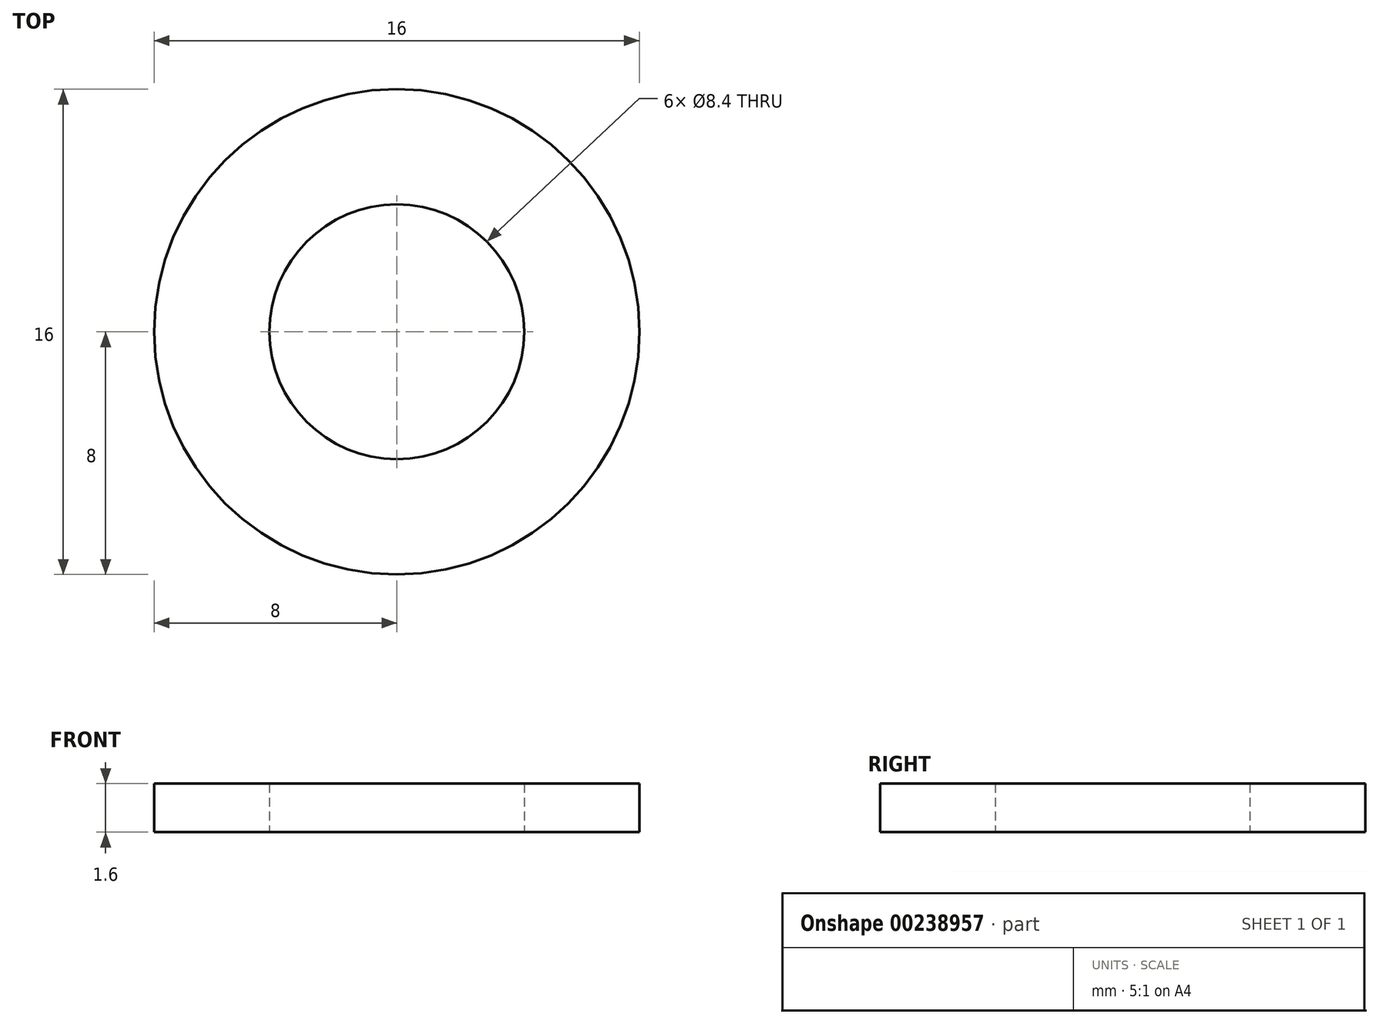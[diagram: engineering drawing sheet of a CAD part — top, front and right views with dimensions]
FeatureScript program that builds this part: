
annotation { "Feature Type Name" : "Feature", "Feature Type Description" : "" }
export const myFeature = defineFeature(function(context is Context, id is Id, definition is map)
    precondition{}
    {
        {
            var Q0;
            Q0=qCreatedBy(makeId("Top.planeOp"),FACE);
            var sketch = newSketch(context, id + "F0", { "sketchPlane" : qUnion([Q0])});
            skCircle(sketch, "E0", {"center": v(0, 0) * mm, "radius": 4.2 * mm});
            skCircle(sketch, "E1", {"center": v(0, 0) * mm, "radius": 8 * mm});
            skSolve(sketch);
        }
        {
            var Q0;
            Q0 = qSketchRegion(id + "F0", true);
            extrude(context, id + "F1", {"entities" : qUnion([Q0]), "depth" : 1.6 * mm});
        }
    });
